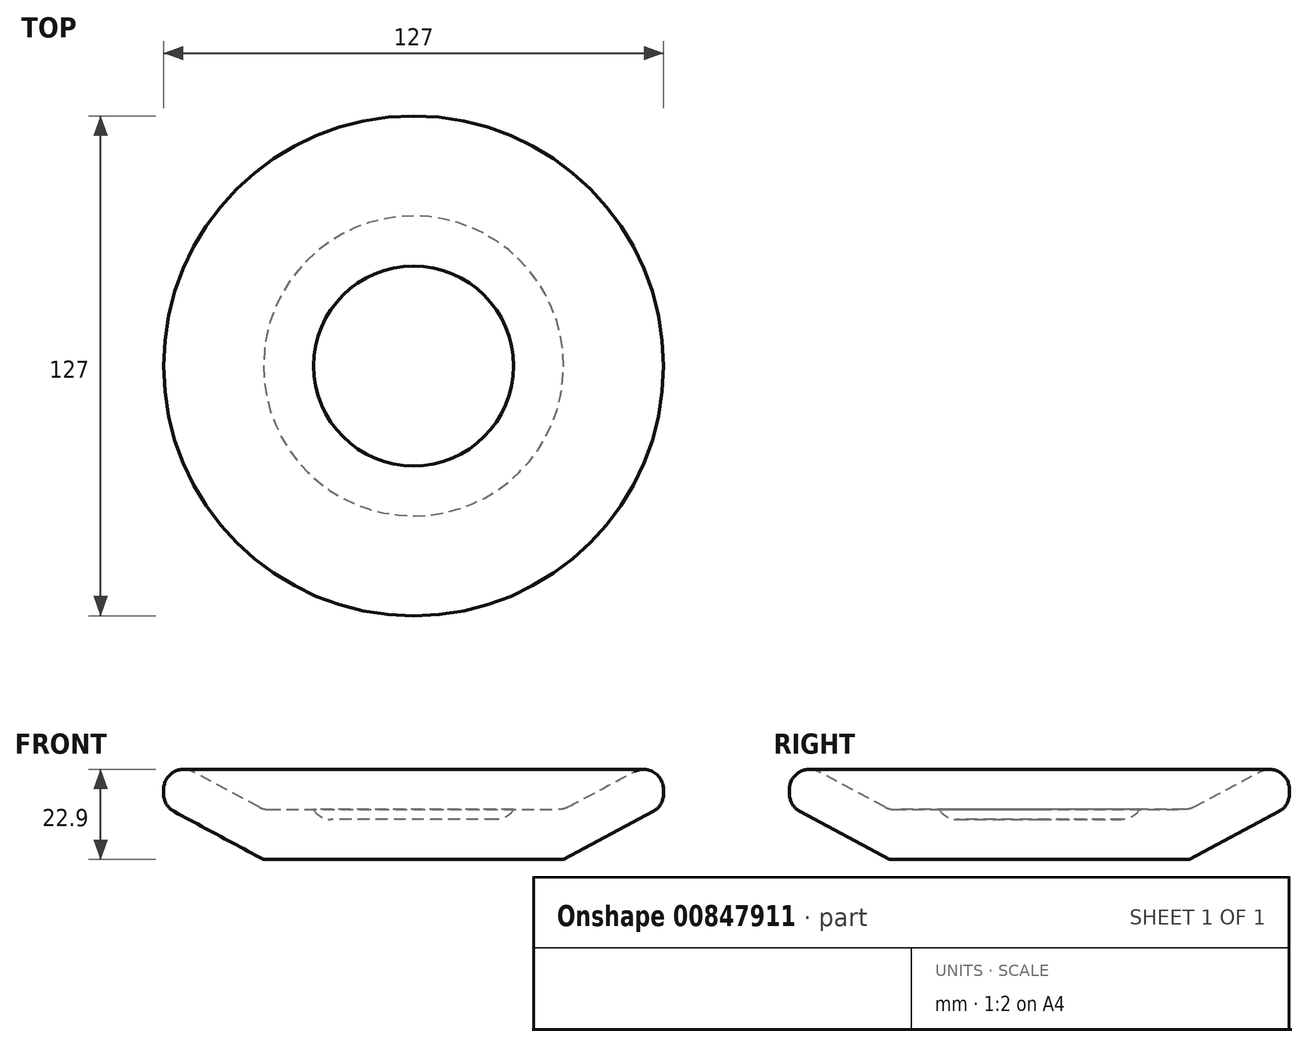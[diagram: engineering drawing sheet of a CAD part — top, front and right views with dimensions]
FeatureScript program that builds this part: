
annotation { "Feature Type Name" : "Feature", "Feature Type Description" : "" }
export const myFeature = defineFeature(function(context is Context, id is Id, definition is map)
    precondition{}
    {
        {
            var Q0;
            Q0=qCreatedBy(makeId("Front.planeOp"),FACE);
            var sketch = newSketch(context, id + "F0", { "sketchPlane" : qUnion([Q0])});
            skLineSegment(sketch, "E0", {"start": v(63.5, 26.3) * mm, "end": v(63.5, 13.6) * mm});
            skLineSegment(sketch, "E1", {"start": v(63.5, 13.6) * mm, "end": v(38.1, 0) * mm});
            skLineSegment(sketch, "E2", {"start": v(38.1, 0) * mm, "end": v(0, 0) * mm});
            skLineSegment(sketch, "E3", {"start": v(0, 12.7) * mm, "end": v(38.1, 12.7) * mm});
            skLineSegment(sketch, "E4", {"start": v(38.1, 12.7) * mm, "end": v(63.5, 26.3) * mm});
            skLineSegment(sketch, "E5", {"start": v(0, 12.7) * mm, "end": v(0, 0) * mm});
            skSolve(sketch);
        }
        {
            var Q0;
            Q0=qCreatedBy(makeId("Front.planeOp"),FACE);
            var sketch = newSketch(context, id + "F1", { "sketchPlane" : qUnion([Q0])});
            skLineSegment(sketch, "E6", {"start": v(0, 0) * mm, "end": v(0, 74.61) * mm, "construction": true});
            skSolve(sketch);
        }
        {
            var Q0;
            Q0=makeQuery(id+"F0.imprint","IMPRINT",FACE,{"disambiguationData":[TD([[makeQuery(id+"F0.imprint","IMPRINT",EDGE,{"derivedFrom":sQuery(id+"F0.wireOp",EDGE,"E0")}),-1.0]])]});
            var Q1;
            Q1=sQuery(id+"F1.wireOp",EDGE,"E6");
            revolve(context, id + "F2", {"surfaceOperationType" : NewSurfaceOperationType.NEW, "entities" : qUnion([Q0]), "axis" : qUnion([Q1]), "revolveType" : RevolveType.FULL});
        }
        {
            var Q0;
            Q0=makeQuery(id+"F2.opRevolve","SWEPT_FACE",FACE,{"disambiguationData":[OSD([sQuery(id+"F0.wireOp",EDGE,"E3")])]});
            var sketch = newSketch(context, id + "F3", { "sketchPlane" : qUnion([Q0])});
            skCircle(sketch, "E7", {"center": v(0, 0) * mm, "radius": 25.4 * mm});
            skSolve(sketch);
        }
        {
            var Q0;
            Q0=makeQuery(id+"F3.imprint","IMPRINT",FACE,{"disambiguationData":[TD([[makeQuery(id+"F3.imprint","IMPRINT",EDGE,{"derivedFrom":sQuery(id+"F3.wireOp",EDGE,"E7")}),1.0]])]});
            extrude(context, id + "F4", {"entities" : qUnion([Q0]), "operationType" : NewBodyOperationType.REMOVE, "oppositeDirection" : true, "depth" : 2.54 * mm, "offsetDistance" : 25.4 * mm});
        }
        {
            var Q0;
            Q0=makeQuery(id+"F2.opRevolve","SWEPT_EDGE",EDGE,{"disambiguationData":[OSD([sQuery(id+"F0.wireOp",EDGE,"E3"),sQuery(id+"F0.wireOp",EDGE,"E4")])]});
            var Q1;
            Q1=makeQuery(id+"F4.boolean.opBoolean","COPY",EDGE,{"derivedFrom":makeQuery(id+"F4.opExtrude","CAP_EDGE",EDGE,{"disambiguationData":[OSD([sQuery(id+"F3.wireOp",EDGE,"E7")])],"isStart":false})});
            var Q2;
            Q2=makeQuery(id+"F2.opRevolve","SWEPT_EDGE",EDGE,{"disambiguationData":[OSD([sQuery(id+"F0.wireOp",EDGE,"E0"),sQuery(id+"F0.wireOp",EDGE,"E4")])]});
            var Q3;
            Q3=makeQuery(id+"F2.opRevolve","SWEPT_EDGE",EDGE,{"disambiguationData":[OSD([sQuery(id+"F0.wireOp",EDGE,"E0"),sQuery(id+"F0.wireOp",EDGE,"E1")])]});
            fillet(context, id + "F5", {"entities" : qUnion([Q0, Q1, Q2, Q3]), "radius" : 5.08 * mm, "tangentPropagation" : true, "allowEdgeOverflow" : false});
        }
    });
